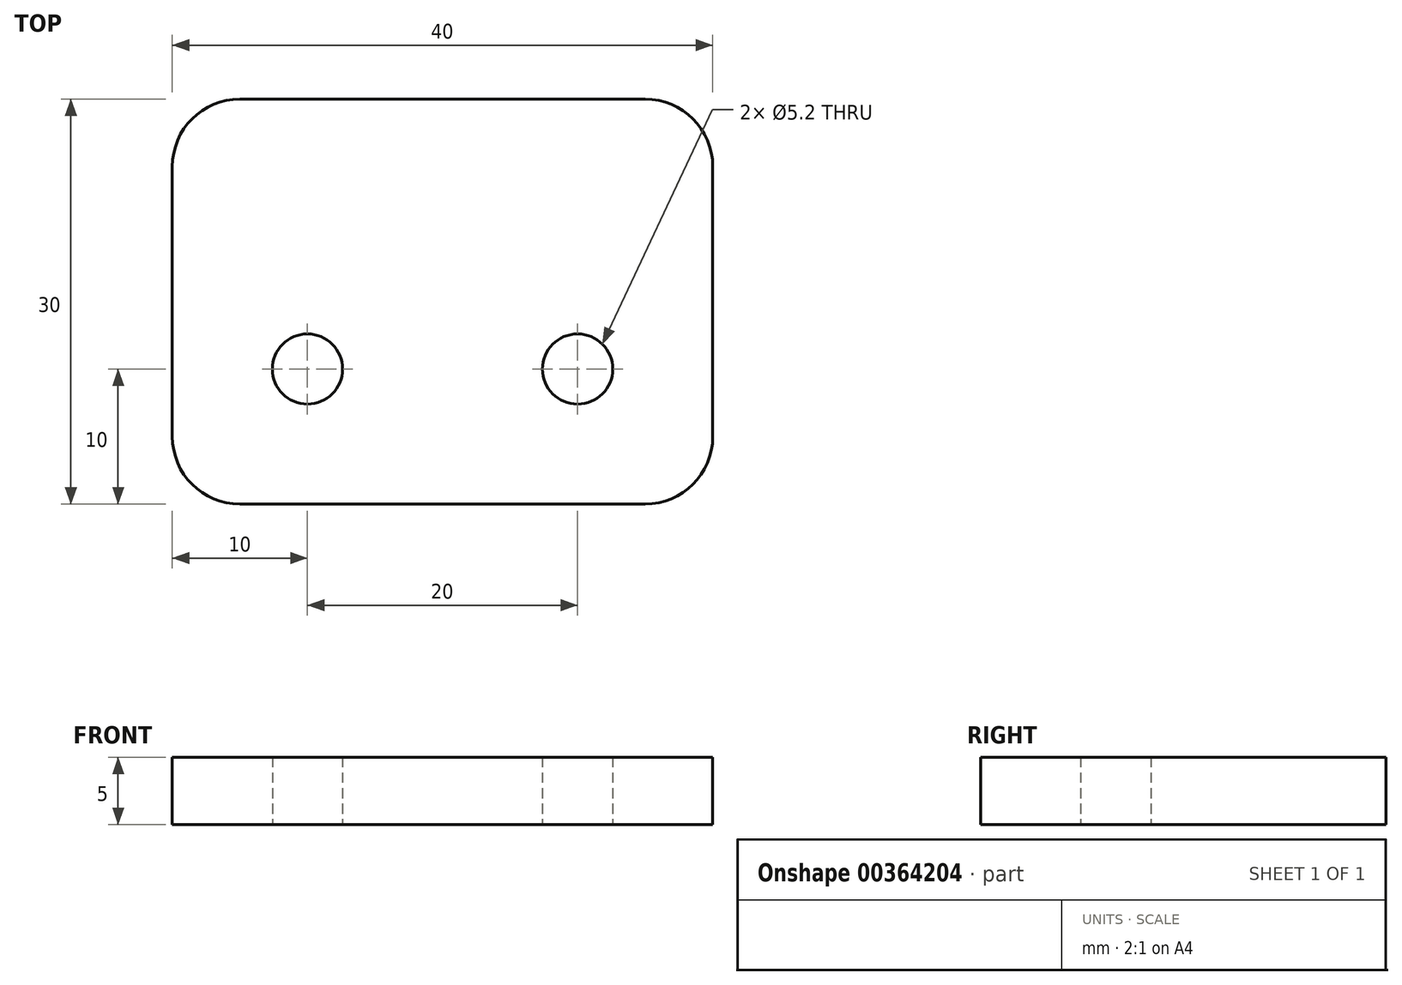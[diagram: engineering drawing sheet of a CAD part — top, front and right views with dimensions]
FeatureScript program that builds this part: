
annotation { "Feature Type Name" : "Feature", "Feature Type Description" : "" }
export const myFeature = defineFeature(function(context is Context, id is Id, definition is map)
    precondition{}
    {
        {
            var Q0;
            Q0=qCreatedBy(makeId("Top.planeOp"),FACE);
            var sketch = newSketch(context, id + "F0", { "sketchPlane" : qUnion([Q0])});
            skLineSegment(sketch, "E0.bottom", {"start": v(15, -15) * mm, "end": v(-15, -15) * mm});
            skLineSegment(sketch, "E0.top", {"start": v(15, 15) * mm, "end": v(-15, 15) * mm});
            skLineSegment(sketch, "E0.left", {"start": v(20, -10) * mm, "end": v(20, 10) * mm});
            skLineSegment(sketch, "E0.right", {"start": v(-20, -10) * mm, "end": v(-20, 10) * mm});
            skPoint(sketch, "E0.middle", {"position": v(0, 0) * mm});
            skPoint(sketch, "E1.visualSharp", {"position": v(-20, 15) * mm});
            skArc(sketch, "E1.filletArc", {"start": v(-15, 15) * mm, "mid": v(-18.54, 13.54) * mm, "end": v(-20, 10) * mm});
            skPoint(sketch, "E2.visualSharp", {"position": v(-20, -15) * mm});
            skArc(sketch, "E2.filletArc", {"start": v(-20, -10) * mm, "mid": v(-18.54, -13.54) * mm, "end": v(-15, -15) * mm});
            skPoint(sketch, "E3.visualSharp", {"position": v(20, 15) * mm});
            skArc(sketch, "E3.filletArc", {"start": v(20, 10) * mm, "mid": v(18.54, 13.54) * mm, "end": v(15, 15) * mm});
            skPoint(sketch, "E4.visualSharp", {"position": v(20, -15) * mm});
            skArc(sketch, "E4.filletArc", {"start": v(15, -15) * mm, "mid": v(18.54, -13.54) * mm, "end": v(20, -10) * mm});
            skLineSegment(sketch, "E5", {"start": v(-27.34, -5) * mm, "end": v(33.99, -5) * mm, "construction": true});
            skCircle(sketch, "E6", {"center": v(-10, -5) * mm, "radius": 2.6 * mm});
            skCircle(sketch, "E7", {"center": v(10, -5) * mm, "radius": 2.6 * mm});
            skSolve(sketch);
        }
        {
            var Q0;
            Q0=makeQuery(id+"F0.imprint","IMPRINT",FACE,{"disambiguationData":[TD([[makeQuery(id+"F0.imprint","IMPRINT",EDGE,{"derivedFrom":sQuery(id+"F0.wireOp",EDGE,"E0.bottom")}),-1.0]])]});
            extrude(context, id + "F1", {"entities" : qUnion([Q0]), "depth" : 5 * mm, "offsetDistance" : 25 * mm});
        }
    });
